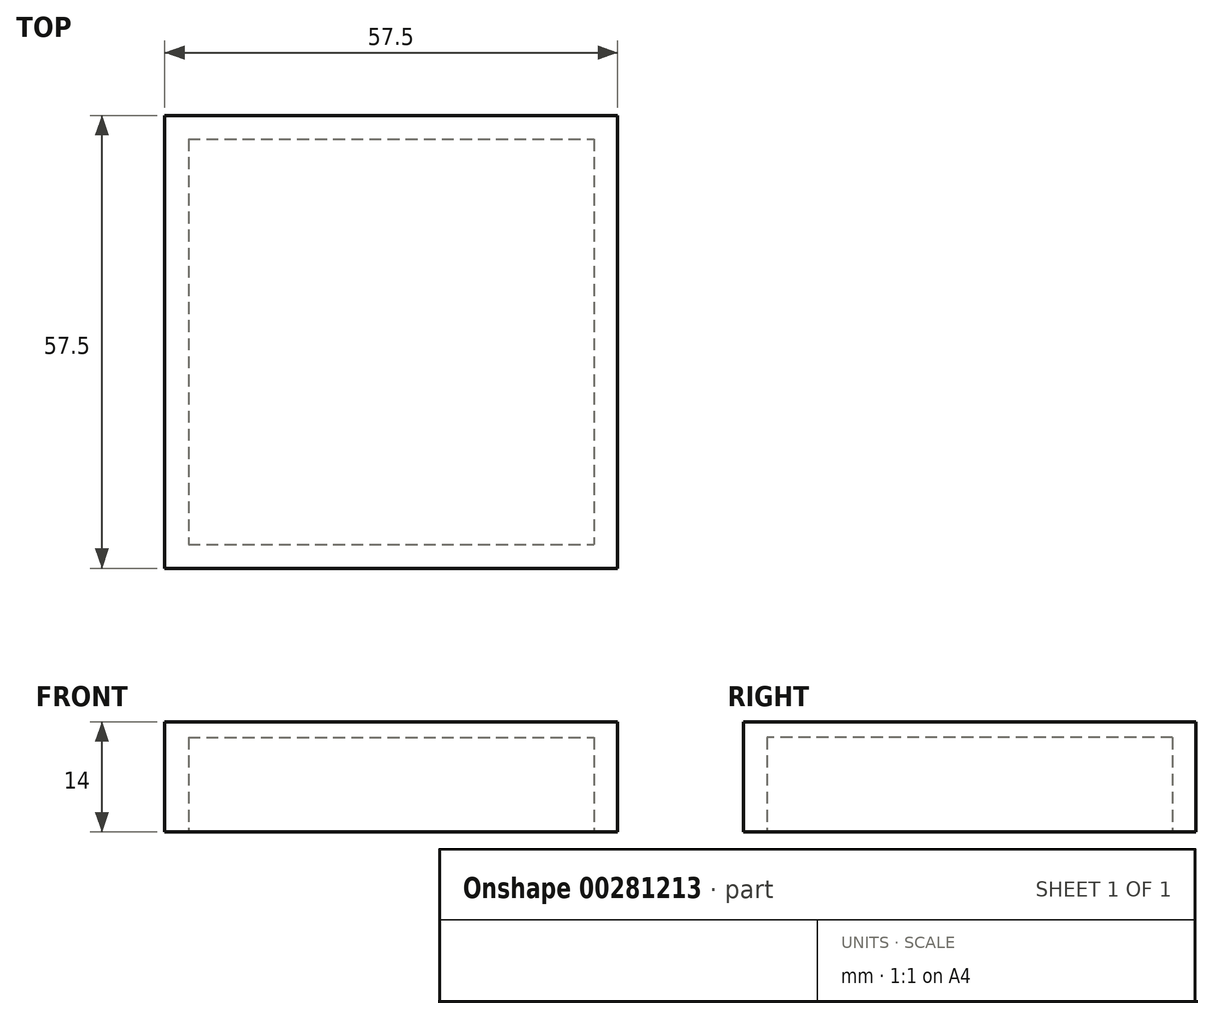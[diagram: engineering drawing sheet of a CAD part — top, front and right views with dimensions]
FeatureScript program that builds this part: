
annotation { "Feature Type Name" : "Feature", "Feature Type Description" : "" }
export const myFeature = defineFeature(function(context is Context, id is Id, definition is map)
    precondition{}
    {
        {
            var Q0;
            Q0=qCreatedBy(makeId("Top.planeOp"),FACE);
            var sketch = newSketch(context, id + "F0", { "sketchPlane" : qUnion([Q0])});
            skLineSegment(sketch, "E0.bottom", {"start": v(-31.37, 29.13) * mm, "end": v(20.13, 29.13) * mm});
            skLineSegment(sketch, "E0.top", {"start": v(-31.37, -22.37) * mm, "end": v(20.13, -22.37) * mm});
            skLineSegment(sketch, "E0.left", {"start": v(-31.37, 29.13) * mm, "end": v(-31.37, -22.37) * mm});
            skLineSegment(sketch, "E0.right", {"start": v(20.13, 29.13) * mm, "end": v(20.13, -22.37) * mm});
            skLineSegment(sketch, "E1.0", {"start": v(-34.37, 32.13) * mm, "end": v(23.13, 32.13) * mm});
            skLineSegment(sketch, "E1.1", {"start": v(-34.37, 32.13) * mm, "end": v(-34.37, -25.37) * mm});
            skLineSegment(sketch, "E1.2", {"start": v(-34.37, -25.37) * mm, "end": v(23.13, -25.37) * mm});
            skLineSegment(sketch, "E1.3", {"start": v(23.13, 32.13) * mm, "end": v(23.13, -25.37) * mm});
            skSolve(sketch);
        }
        {
            var Q0;
            Q0 = qSketchRegion(id + "F0", true);
            extrude(context, id + "F1", {"entities" : qUnion([Q0]), "depth" : 12 * mm});
        }
        {
            var Q0;
            Q0=makeQuery(id+"F1.opExtrude","CAP_FACE",FACE,{"disambiguationData":[OSD([sQuery(id+"F0.wireOp",EDGE,"E0.bottom"),sQuery(id+"F0.wireOp",EDGE,"E0.top"),sQuery(id+"F0.wireOp",EDGE,"E0.left"),sQuery(id+"F0.wireOp",EDGE,"E0.right"),sQuery(id+"F0.wireOp",EDGE,"E1.0"),sQuery(id+"F0.wireOp",EDGE,"E1.1"),sQuery(id+"F0.wireOp",EDGE,"E1.2"),sQuery(id+"F0.wireOp",EDGE,"E1.3")])],"isStart":false});
            var sketch = newSketch(context, id + "F2", { "sketchPlane" : qUnion([Q0])});
            skLineSegment(sketch, "E2.bottom", {"start": v(-34.37, 32.13) * mm, "end": v(23.13, 32.13) * mm});
            skLineSegment(sketch, "E2.top", {"start": v(-34.37, -25.37) * mm, "end": v(23.13, -25.37) * mm});
            skLineSegment(sketch, "E2.left", {"start": v(-34.37, 32.13) * mm, "end": v(-34.37, -25.37) * mm});
            skLineSegment(sketch, "E2.right", {"start": v(23.13, 32.13) * mm, "end": v(23.13, -25.37) * mm});
            skSolve(sketch);
        }
        {
            var Q0;
            Q0 = qSketchRegion(id + "F2", true);
            extrude(context, id + "F3", {"entities" : qUnion([Q0]), "operationType" : NewBodyOperationType.ADD, "depth" : 2 * mm});
        }
    });
